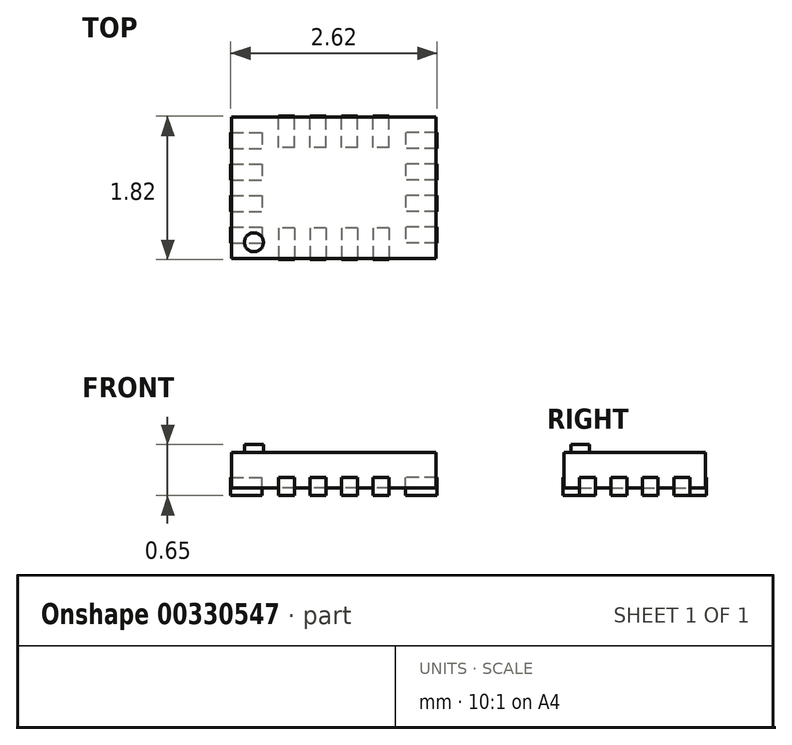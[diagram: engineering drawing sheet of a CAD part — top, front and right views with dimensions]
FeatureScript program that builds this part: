
annotation { "Feature Type Name" : "Feature", "Feature Type Description" : "" }
export const myFeature = defineFeature(function(context is Context, id is Id, definition is map)
    precondition{}
    {
        {
            var Q0;
            Q0=qCreatedBy(makeId("Top.planeOp"),FACE);
            var sketch = newSketch(context, id + "F0", { "sketchPlane" : qUnion([Q0])});
            skLineSegment(sketch, "E0.bottom", {"start": v(1.3, -0.9) * mm, "end": v(-1.3, -0.9) * mm});
            skLineSegment(sketch, "E0.top", {"start": v(1.3, 0.9) * mm, "end": v(-1.3, 0.9) * mm});
            skLineSegment(sketch, "E0.left", {"start": v(1.3, -0.9) * mm, "end": v(1.3, 0.9) * mm});
            skLineSegment(sketch, "E0.right", {"start": v(-1.3, -0.9) * mm, "end": v(-1.3, 0.9) * mm});
            skPoint(sketch, "E0.middle", {"position": v(0, 0) * mm});
            skSolve(sketch);
        }
        {
            var Q0;
            Q0 = qSketchRegion(id + "F0", true);
            extrude(context, id + "F1", {"entities" : qUnion([Q0]), "depth" : .45 * mm, "offsetDistance" : 25 * mm});
        }
        {
            var Q0;
            Q0=makeQuery(id+"F1.opExtrude","CAP_FACE",FACE,{"disambiguationData":[OSD([sQuery(id+"F0.wireOp",EDGE,"E0.bottom"),sQuery(id+"F0.wireOp",EDGE,"E0.top"),sQuery(id+"F0.wireOp",EDGE,"E0.left"),sQuery(id+"F0.wireOp",EDGE,"E0.right")])],"isStart":true});
            var sketch = newSketch(context, id + "F2", { "sketchPlane" : qUnion([Q0])});
            skLineSegment(sketch, "E1", {"start": v(0, 0.9) * mm, "end": v(0, -0.9) * mm, "construction": true});
            skLineSegment(sketch, "E2", {"start": v(-1.3, 0) * mm, "end": v(1.3, 0) * mm, "construction": true});
            skLineSegment(sketch, "E3.bottom", {"start": v(-0.5, 0.51) * mm, "end": v(-0.7, 0.51) * mm});
            skLineSegment(sketch, "E3.top", {"start": v(-0.5, 0.91) * mm, "end": v(-0.7, 0.91) * mm});
            skLineSegment(sketch, "E3.left", {"start": v(-0.5, 0.51) * mm, "end": v(-0.5, 0.91) * mm});
            skLineSegment(sketch, "E3.right", {"start": v(-0.7, 0.51) * mm, "end": v(-0.7, 0.91) * mm});
            skPoint(sketch, "E3.middle", {"position": v(-0.6, 0.71) * mm});
            skLineSegment(sketch, "E4.1.0.0", {"start": v(-0.1, 0.91) * mm, "end": v(-0.3, 0.91) * mm});
            skLineSegment(sketch, "E4.1.0.1", {"start": v(-0.1, 0.51) * mm, "end": v(-0.1, 0.91) * mm});
            skLineSegment(sketch, "E4.1.0.2", {"start": v(-0.1, 0.51) * mm, "end": v(-0.3, 0.51) * mm});
            skLineSegment(sketch, "E4.1.0.3", {"start": v(-0.3, 0.51) * mm, "end": v(-0.3, 0.91) * mm});
            skPoint(sketch, "E4.1.0.4", {"position": v(-0.2, 0.71) * mm});
            skLineSegment(sketch, "E4.2.0.0", {"start": v(0.3, 0.91) * mm, "end": v(0.1, 0.91) * mm});
            skLineSegment(sketch, "E4.2.0.1", {"start": v(0.3, 0.51) * mm, "end": v(0.3, 0.91) * mm});
            skLineSegment(sketch, "E4.2.0.2", {"start": v(0.3, 0.51) * mm, "end": v(0.1, 0.51) * mm});
            skLineSegment(sketch, "E4.2.0.3", {"start": v(0.1, 0.51) * mm, "end": v(0.1, 0.91) * mm});
            skPoint(sketch, "E4.2.0.4", {"position": v(0.2, 0.71) * mm});
            skLineSegment(sketch, "E4.3.0.0", {"start": v(0.7, 0.91) * mm, "end": v(0.5, 0.91) * mm});
            skLineSegment(sketch, "E4.3.0.1", {"start": v(0.7, 0.51) * mm, "end": v(0.7, 0.91) * mm});
            skLineSegment(sketch, "E4.3.0.2", {"start": v(0.7, 0.51) * mm, "end": v(0.5, 0.51) * mm});
            skLineSegment(sketch, "E4.3.0.3", {"start": v(0.5, 0.51) * mm, "end": v(0.5, 0.91) * mm});
            skPoint(sketch, "E4.3.0.4", {"position": v(0.6, 0.71) * mm});
            skLineSegment(sketch, "E4.direction1", {"start": v(-0.7, 0.51) * mm, "end": v(-0.3, 0.51) * mm, "construction": true});
            skLineSegment(sketch, "E5.MirrorCS", {"start": v(-0.5, -0.5) * mm, "end": v(-0.7, -0.5) * mm});
            skLineSegment(sketch, "E6.MirrorCS", {"start": v(-0.1, -0.51) * mm, "end": v(-0.1, -0.91) * mm});
            skLineSegment(sketch, "E7.MirrorCS", {"start": v(-0.1, -0.51) * mm, "end": v(-0.3, -0.51) * mm});
            skLineSegment(sketch, "E8.MirrorCS", {"start": v(-0.3, -0.51) * mm, "end": v(-0.3, -0.9) * mm});
            skLineSegment(sketch, "E9.MirrorCS", {"start": v(0.3, -0.91) * mm, "end": v(0.1, -0.91) * mm});
            skLineSegment(sketch, "E10.MirrorCS", {"start": v(0.3, -0.51) * mm, "end": v(0.3, -0.91) * mm});
            skLineSegment(sketch, "E11.MirrorCS", {"start": v(0.3, -0.51) * mm, "end": v(0.1, -0.51) * mm});
            skLineSegment(sketch, "E12.MirrorCS", {"start": v(-0.7, -0.5) * mm, "end": v(-0.3, -0.51) * mm, "construction": true});
            skPoint(sketch, "E13.MirrorP", {"position": v(0.6, -0.71) * mm});
            skPoint(sketch, "E14.MirrorP", {"position": v(-0.2, -0.71) * mm});
            skLineSegment(sketch, "E15.MirrorCS", {"start": v(0.7, -0.51) * mm, "end": v(0.5, -0.51) * mm});
            skPoint(sketch, "E16.MirrorP", {"position": v(0.2, -0.71) * mm});
            skLineSegment(sketch, "E17.MirrorCS", {"start": v(0.5, -0.51) * mm, "end": v(0.5, -0.91) * mm});
            skPoint(sketch, "E18.MirrorP", {"position": v(-0.6, -0.71) * mm});
            skLineSegment(sketch, "E19.MirrorCS", {"start": v(0.1, -0.51) * mm, "end": v(0.1, -0.91) * mm});
            skLineSegment(sketch, "E20.MirrorCS", {"start": v(-0.1, -0.9) * mm, "end": v(-0.3, -0.9) * mm});
            skLineSegment(sketch, "E21.MirrorCS", {"start": v(0.7, -0.91) * mm, "end": v(0.5, -0.91) * mm});
            skLineSegment(sketch, "E22.MirrorCS", {"start": v(0.7, -0.51) * mm, "end": v(0.7, -0.91) * mm});
            skLineSegment(sketch, "E23.MirrorCS", {"start": v(0, -0.9) * mm, "end": v(0, 0.9) * mm, "construction": true});
            skLineSegment(sketch, "E24.MirrorCS", {"start": v(-0.7, -0.5) * mm, "end": v(-0.7, -0.9) * mm});
            skLineSegment(sketch, "E25.MirrorCS", {"start": v(-0.5, -0.51) * mm, "end": v(-0.5, -0.9) * mm});
            skLineSegment(sketch, "E26.MirrorCS", {"start": v(-0.5, -0.9) * mm, "end": v(-0.7, -0.9) * mm});
            skLineSegment(sketch, "E27.bottom", {"start": v(1.31, 0.5) * mm, "end": v(0.91, 0.5) * mm});
            skLineSegment(sketch, "E27.top", {"start": v(1.31, 0.7) * mm, "end": v(0.91, 0.7) * mm});
            skLineSegment(sketch, "E27.left", {"start": v(1.31, 0.5) * mm, "end": v(1.31, 0.7) * mm});
            skLineSegment(sketch, "E27.right", {"start": v(0.91, 0.5) * mm, "end": v(0.91, 0.7) * mm});
            skPoint(sketch, "E27.middle", {"position": v(1.11, 0.6) * mm});
            skLineSegment(sketch, "E28.0.1.0", {"start": v(1.31, 0.1) * mm, "end": v(0.91, 0.1) * mm});
            skLineSegment(sketch, "E28.0.1.1", {"start": v(1.31, 0.3) * mm, "end": v(0.91, 0.3) * mm});
            skPoint(sketch, "E28.0.1.2", {"position": v(1.11, 0.2) * mm});
            skLineSegment(sketch, "E28.0.1.3", {"start": v(1.31, 0.1) * mm, "end": v(1.31, 0.3) * mm});
            skLineSegment(sketch, "E28.0.1.4", {"start": v(0.91, 0.1) * mm, "end": v(0.91, 0.3) * mm});
            skLineSegment(sketch, "E28.0.2.0", {"start": v(1.31, -0.3) * mm, "end": v(0.91, -0.3) * mm});
            skLineSegment(sketch, "E28.0.2.1", {"start": v(1.31, -0.1) * mm, "end": v(0.91, -0.1) * mm});
            skPoint(sketch, "E28.0.2.2", {"position": v(1.11, -0.2) * mm});
            skLineSegment(sketch, "E28.0.2.3", {"start": v(1.31, -0.3) * mm, "end": v(1.31, -0.1) * mm});
            skLineSegment(sketch, "E28.0.2.4", {"start": v(0.91, -0.3) * mm, "end": v(0.91, -0.1) * mm});
            skLineSegment(sketch, "E28.0.3.0", {"start": v(1.31, -0.7) * mm, "end": v(0.91, -0.7) * mm});
            skLineSegment(sketch, "E28.0.3.1", {"start": v(1.31, -0.5) * mm, "end": v(0.91, -0.5) * mm});
            skPoint(sketch, "E28.0.3.2", {"position": v(1.11, -0.6) * mm});
            skLineSegment(sketch, "E28.0.3.3", {"start": v(1.31, -0.7) * mm, "end": v(1.31, -0.5) * mm});
            skLineSegment(sketch, "E28.0.3.4", {"start": v(0.91, -0.7) * mm, "end": v(0.91, -0.5) * mm});
            skLineSegment(sketch, "E28.direction1", {"start": v(0.91, 0.5) * mm, "end": v(1.97, 0.5) * mm, "construction": true});
            skLineSegment(sketch, "E28.direction2", {"start": v(0.91, 0.5) * mm, "end": v(0.91, 0.1) * mm, "construction": true});
            skLineSegment(sketch, "E29.MirrorCS", {"start": v(-0.91, 0.1) * mm, "end": v(-0.91, 0.3) * mm});
            skLineSegment(sketch, "E30.MirrorCS", {"start": v(-1.31, 0.5) * mm, "end": v(-0.91, 0.5) * mm});
            skLineSegment(sketch, "E31.MirrorCS", {"start": v(-1.31, 0.1) * mm, "end": v(-1.31, 0.3) * mm});
            skLineSegment(sketch, "E32.MirrorCS", {"start": v(-0.91, -0.3) * mm, "end": v(-0.91, -0.1) * mm});
            skLineSegment(sketch, "E33.MirrorCS", {"start": v(-1.31, 0.5) * mm, "end": v(-1.31, 0.7) * mm});
            skLineSegment(sketch, "E34.MirrorCS", {"start": v(-1.31, 0.7) * mm, "end": v(-0.91, 0.7) * mm});
            skLineSegment(sketch, "E35.MirrorCS", {"start": v(-1.31, -0.1) * mm, "end": v(-0.91, -0.1) * mm});
            skLineSegment(sketch, "E36.MirrorCS", {"start": v(-1.31, -0.3) * mm, "end": v(-1.31, -0.1) * mm});
            skLineSegment(sketch, "E37.MirrorCS", {"start": v(-1.31, -0.7) * mm, "end": v(-0.91, -0.7) * mm});
            skLineSegment(sketch, "E38.MirrorCS", {"start": v(-1.31, 0.1) * mm, "end": v(-0.91, 0.1) * mm});
            skLineSegment(sketch, "E39.MirrorCS", {"start": v(-1.31, -0.3) * mm, "end": v(-0.91, -0.3) * mm});
            skLineSegment(sketch, "E40.MirrorCS", {"start": v(-0.91, -0.7) * mm, "end": v(-0.91, -0.5) * mm});
            skLineSegment(sketch, "E41.MirrorCS", {"start": v(-1.31, 0.3) * mm, "end": v(-0.91, 0.3) * mm});
            skLineSegment(sketch, "E42.MirrorCS", {"start": v(-0.91, 0.5) * mm, "end": v(-1.97, 0.5) * mm, "construction": true});
            skLineSegment(sketch, "E43.MirrorCS", {"start": v(1.3, 0) * mm, "end": v(-1.3, 0) * mm, "construction": true});
            skPoint(sketch, "E44.MirrorP", {"position": v(-1.11, -0.6) * mm});
            skLineSegment(sketch, "E45.MirrorCS", {"start": v(-1.31, -0.7) * mm, "end": v(-1.31, -0.5) * mm});
            skPoint(sketch, "E46.MirrorP", {"position": v(-1.11, -0.2) * mm});
            skPoint(sketch, "E47.MirrorP", {"position": v(-1.11, 0.2) * mm});
            skLineSegment(sketch, "E48.MirrorCS", {"start": v(-0.91, 0.5) * mm, "end": v(-0.91, 0.1) * mm, "construction": true});
            skPoint(sketch, "E49.MirrorP", {"position": v(-1.11, 0.6) * mm});
            skLineSegment(sketch, "E50.MirrorCS", {"start": v(-0.91, 0.5) * mm, "end": v(-0.91, 0.7) * mm});
            skLineSegment(sketch, "E51.MirrorCS", {"start": v(-1.31, -0.5) * mm, "end": v(-0.91, -0.5) * mm});
            skSolve(sketch);
        }
        {
            var Q0;
            Q0 = qSketchRegion(id + "F2", true);
            extrude(context, id + "F3", {"entities" : qUnion([Q0]), "depth" : .1 * mm, "offsetDistance" : 25 * mm, "hasSecondDirection" : true, "secondDirectionOppositeDirection" : true, "secondDirectionDepth" : .13 * mm});
        }
        {
            var Q0;
            Q0=makeQuery(id+"F1.opExtrude","CAP_FACE",FACE,{"disambiguationData":[OSD([sQuery(id+"F0.wireOp",EDGE,"E0.bottom"),sQuery(id+"F0.wireOp",EDGE,"E0.top"),sQuery(id+"F0.wireOp",EDGE,"E0.left"),sQuery(id+"F0.wireOp",EDGE,"E0.right")])],"isStart":false});
            var sketch = newSketch(context, id + "F4", { "sketchPlane" : qUnion([Q0])});
            skCircle(sketch, "E52", {"center": v(-1.01, -0.7) * mm, "radius": 0.12 * mm});
            skSolve(sketch);
        }
        {
            var Q0;
            Q0 = qSketchRegion(id + "F4", true);
            extrude(context, id + "F5", {"entities" : qUnion([Q0]), "depth" : .1 * mm, "offsetDistance" : 25 * mm});
        }
    });
